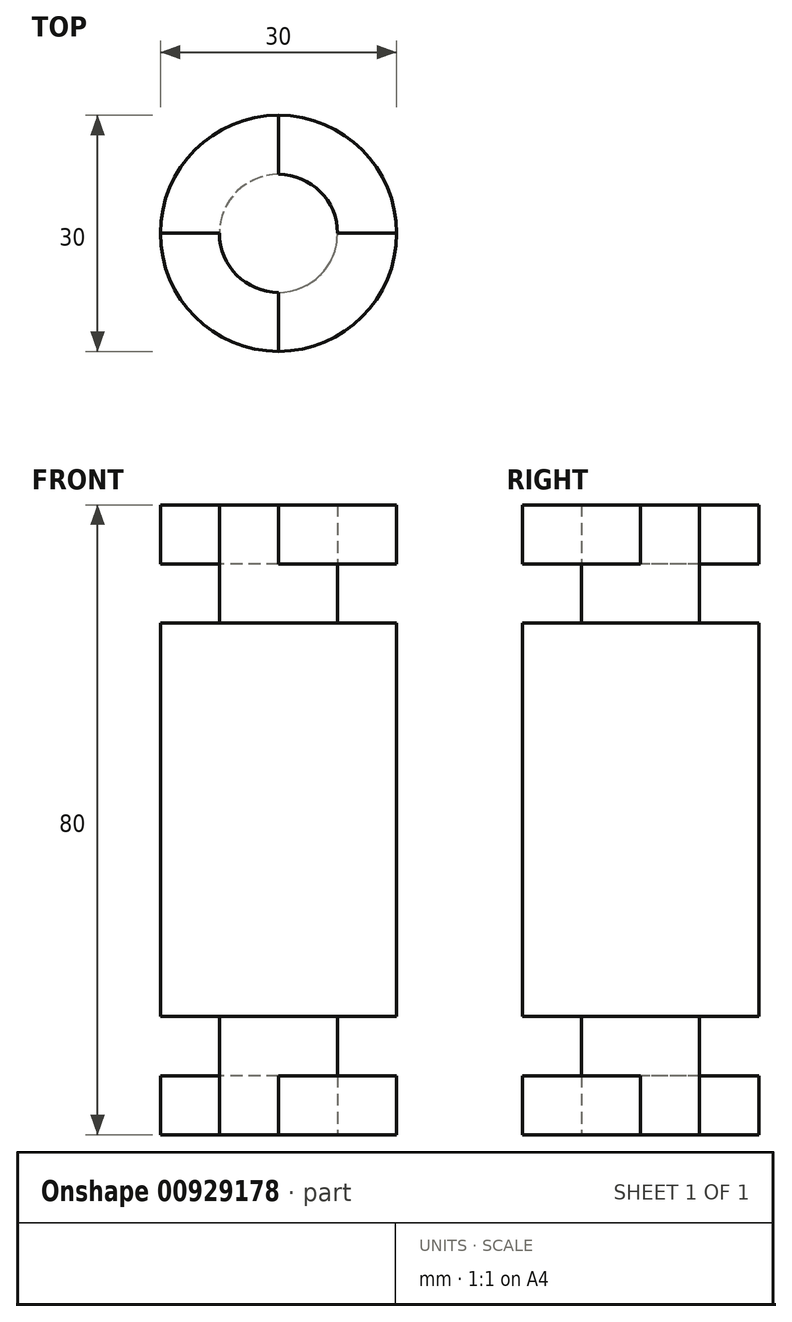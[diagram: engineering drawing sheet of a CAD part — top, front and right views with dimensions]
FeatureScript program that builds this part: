
annotation { "Feature Type Name" : "Feature", "Feature Type Description" : "" }
export const myFeature = defineFeature(function(context is Context, id is Id, definition is map)
    precondition{}
    {
        {
            var Q0;
            Q0=qCreatedBy(makeId("Top.planeOp"),FACE);
            var sketch = newSketch(context, id + "F0", { "sketchPlane" : qUnion([Q0])});
            skCircle(sketch, "E0", {"center": v(0, 0) * mm, "radius": 15 * mm});
            skArc(sketch, "E1", {"start": v(0, 7.5) * mm, "mid": v(-5.3, 5.3) * mm, "end": v(-7.5, 0) * mm});
            skLineSegment(sketch, "E2", {"start": v(0, 15) * mm, "end": v(0, 7.5) * mm});
            skLineSegment(sketch, "E3", {"start": v(-15, 0) * mm, "end": v(-7.5, 0) * mm});
            skLineSegment(sketch, "E4.trimOffspring", {"start": v(7.5, 0) * mm, "end": v(15, 0) * mm});
            skLineSegment(sketch, "E5.trimOffspring", {"start": v(0, -7.5) * mm, "end": v(0, -15) * mm});
            skArc(sketch, "E6.trimOffspring", {"start": v(0, -7.5) * mm, "mid": v(5.3, -5.3) * mm, "end": v(7.5, 0) * mm});
            skCircle(sketch, "E7", {"center": v(0, 0) * mm, "radius": 7.5 * mm});
            skSolve(sketch);
        }
        {
            var Q0;
            {var subQ0=sQuery(id+"F0.wireOp",EDGE,"E2");Q0=makeQuery(id+"F0.imprint","IMPRINT",FACE,{"disambiguationData":[TD([[makeQuery(id+"F0.imprint","IMPRINT",EDGE,{"derivedFrom":subQ0}),-1.0]])]});}
            var Q1;
            {var subQ0=sQuery(id+"F0.wireOp",EDGE,"E4.trimOffspring");Q1=makeQuery(id+"F0.imprint","IMPRINT",FACE,{"disambiguationData":[TD([[makeQuery(id+"F0.imprint","IMPRINT",EDGE,{"derivedFrom":subQ0}),-1.0]])]});}
            var Q2;
            {var subQ0=sQuery(id+"F0.wireOp",EDGE,"E7");var subQ1=makeQuery(id+"F0.imprint","INTERSECT",VERTEX,{"derivedFrom":[sQuery(id+"F0.wireOp",EDGE,"E2"),subQ0]});Q2=makeQuery(id+"F0.imprint","IMPRINT",FACE,{"disambiguationData":[TD([[makeQuery(id+"F0.imprint","IMPRINT",EDGE,{"disambiguationData":[TD([[subQ1,1.0]])],"derivedFrom":subQ0}),1.0]])]});}
            extrude(context, id + "F1", {"entities" : qUnion([Q0, Q1, Q2]), "endBound" : BoundingType.SYMMETRIC, "depth" : 80 * mm, "offsetDistance" : 25 * mm});
        }
        {
            var Q0;
            {var subQ0=sQuery(id+"F0.wireOp",EDGE,"E2");Q0=makeQuery(id+"F0.imprint","IMPRINT",FACE,{"disambiguationData":[TD([[makeQuery(id+"F0.imprint","IMPRINT",EDGE,{"derivedFrom":subQ0}),-1.0]])]});}
            var Q1;
            {var subQ0=sQuery(id+"F0.wireOp",EDGE,"E4.trimOffspring");Q1=makeQuery(id+"F0.imprint","IMPRINT",FACE,{"disambiguationData":[TD([[makeQuery(id+"F0.imprint","IMPRINT",EDGE,{"derivedFrom":subQ0}),-1.0]])]});}
            extrude(context, id + "F2", {"entities" : qUnion([Q0, Q1]), "operationType" : NewBodyOperationType.REMOVE, "endBound" : BoundingType.SYMMETRIC, "depth" : 65 * mm, "offsetDistance" : 25 * mm});
        }
        {
            var Q0;
            {var subQ0=sQuery(id+"F0.wireOp",EDGE,"E2");Q0=makeQuery(id+"F0.imprint","IMPRINT",FACE,{"disambiguationData":[TD([[makeQuery(id+"F0.imprint","IMPRINT",EDGE,{"derivedFrom":subQ0}),-1.0]])]});}
            var Q1;
            {var subQ0=sQuery(id+"F0.wireOp",EDGE,"E3");Q1=makeQuery(id+"F0.imprint","IMPRINT",FACE,{"disambiguationData":[TD([[makeQuery(id+"F0.imprint","IMPRINT",EDGE,{"derivedFrom":subQ0}),-1.0]])]});}
            var Q2;
            {var subQ0=sQuery(id+"F0.wireOp",EDGE,"E2");Q2=makeQuery(id+"F0.imprint","IMPRINT",FACE,{"disambiguationData":[TD([[makeQuery(id+"F0.imprint","IMPRINT",EDGE,{"derivedFrom":subQ0}),1.0]])]});}
            var Q3;
            {var subQ0=sQuery(id+"F0.wireOp",EDGE,"E4.trimOffspring");Q3=makeQuery(id+"F0.imprint","IMPRINT",FACE,{"disambiguationData":[TD([[makeQuery(id+"F0.imprint","IMPRINT",EDGE,{"derivedFrom":subQ0}),-1.0]])]});}
            extrude(context, id + "F3", {"entities" : qUnion([Q0, Q1, Q2, Q3]), "operationType" : NewBodyOperationType.ADD, "endBound" : BoundingType.SYMMETRIC, "depth" : 50 * mm, "offsetDistance" : 25 * mm});
        }
    });
